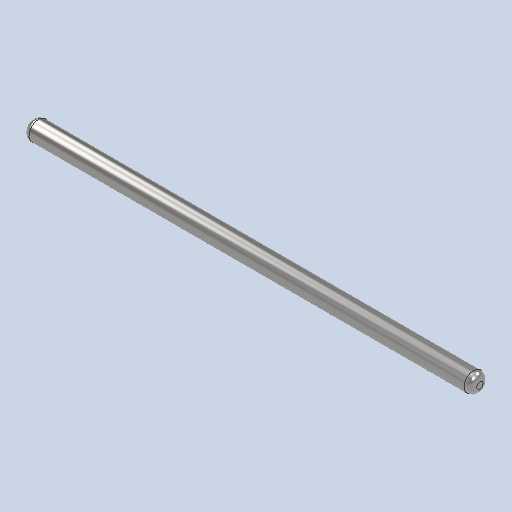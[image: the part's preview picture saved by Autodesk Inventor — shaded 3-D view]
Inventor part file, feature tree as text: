
AUTODESK INVENTOR PART (.ipt)
format: ipt  version: 2022 (Build 260153070, 153G)  size: 103,424 bytes
history: native  units: mm
features: sketch x3, extrude x1, fillet x1
ambient origin geometry x8: Origin, YZ Plane, XZ Plane, XY Plane, X Axis, Y Axis, Z Axis, Center Point
bodies: Solid1 (feature_tree)
feature tree (5):
  extrude  "Extrusion1"  Depth=139.7mm TaperAngle=0.0deg
  sketch  "Sketch2"
  fillet  "Fillet1"  Radius=2.0mm
  sketch  "Sketch3"
  sketch  "Sketch1"  dims[d0=6.0mm d1=139.7mm d2=0.0mm d3=2.0mm]
